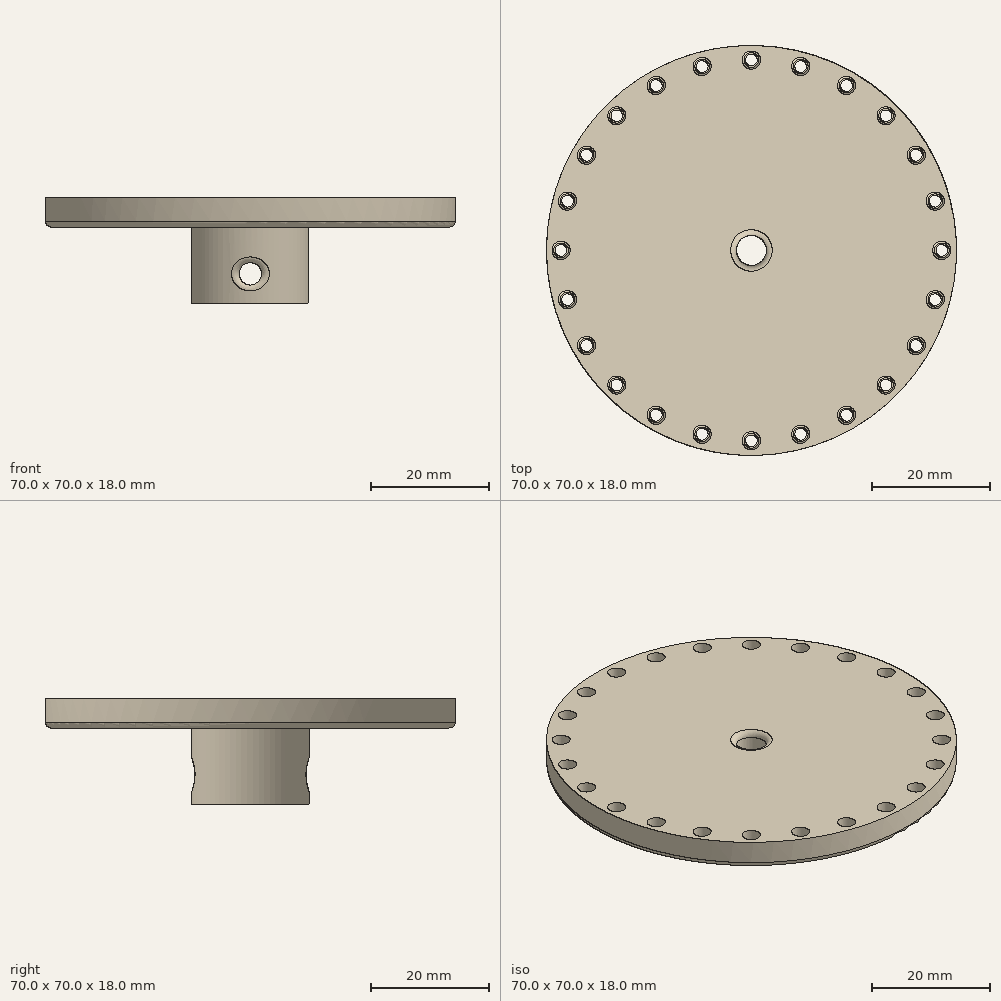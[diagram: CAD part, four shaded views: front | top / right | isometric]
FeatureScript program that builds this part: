
annotation { "Feature Type Name" : "Feature", "Feature Type Description" : "" }
export const myFeature = defineFeature(function(context is Context, id is Id, definition is map)
    precondition{}
    {
        {
            var Q0;
            Q0=qCreatedBy(makeId("Front.planeOp"),FACE);
            var sketch = newSketch(context, id + "F0", { "sketchPlane" : qUnion([Q0])});
            skLineSegment(sketch, "E0", {"start": v(0, 0) * mm, "end": v(0, 18) * mm, "construction": true});
            skLineSegment(sketch, "E1", {"start": v(0, 18) * mm, "end": v(35, 18) * mm});
            skLineSegment(sketch, "E2", {"start": v(35, 18) * mm, "end": v(35, 13) * mm});
            skLineSegment(sketch, "E3", {"start": v(35, 13) * mm, "end": v(10, 13) * mm});
            skLineSegment(sketch, "E4", {"start": v(10, 13) * mm, "end": v(10, 0) * mm});
            skLineSegment(sketch, "E5", {"start": v(10, 0) * mm, "end": v(0, 0) * mm});
            skLineSegment(sketch, "E6", {"start": v(0, 0) * mm, "end": v(0, 18) * mm});
            skSolve(sketch);
        }
        {
            var Q0;
            Q0=makeQuery(id+"F0.imprint","IMPRINT",FACE,{"disambiguationData":[TD([[makeQuery(id+"F0.imprint","IMPRINT",EDGE,{"derivedFrom":sQuery(id+"F0.wireOp",EDGE,"E1")}),-1.0]])]});
            var Q1;
            Q1=sQuery(id+"F0.wireOp",EDGE,"E6");
            revolve(context, id + "F1", {"entities" : qUnion([Q0]), "axis" : qUnion([Q1]), "revolveType" : RevolveType.FULL});
        }
        {
            var Q0;
            Q0=qCreatedBy(makeId("Front.planeOp"),FACE);
            var sketch = newSketch(context, id + "F2", { "sketchPlane" : qUnion([Q0])});
            skCircle(sketch, "E7", {"center": v(0, 5) * mm, "radius": 1.9 * mm});
            skSolve(sketch);
        }
        {
            var Q0;
            Q0 = qSketchRegion(id + "F2", true);
            extrude(context, id + "F3", {"entities" : qUnion([Q0]), "operationType" : NewBodyOperationType.REMOVE, "oppositeDirection" : true, "depth" : 25 * mm, "symmetric" : true});
        }
        {
            var Q0;
            Q0=makeQuery(id+"F1.opRevolve","SWEPT_FACE",FACE,{"disambiguationData":[OSD([sQuery(id+"F0.wireOp",EDGE,"E5")])]});
            var sketch = newSketch(context, id + "F4", { "sketchPlane" : qUnion([Q0])});
            skCircle(sketch, "E8", {"center": v(0, 0) * mm, "radius": 2.55 * mm});
            skSolve(sketch);
        }
        {
            var Q0;
            Q0 = qSketchRegion(id + "F4", true);
            extrude(context, id + "F5", {"entities" : qUnion([Q0]), "operationType" : NewBodyOperationType.REMOVE, "endBound" : BoundingType.THROUGH_ALL, "oppositeDirection" : true, "depth" : 25 * mm});
        }
        {
            var Q0;
            Q0=makeQuery(id+"F5.boolean.opBoolean","COPY",EDGE,{"derivedFrom":makeQuery(id+"F5.opExtrude","CAP_EDGE",EDGE,{"disambiguationData":[OSD([sQuery(id+"F4.wireOp",EDGE,"E8")])],"isStart":true})});
            var Q1;
            Q1=makeQuery(id+"F5.boolean.opBoolean","INTERSECT",EDGE,{"derivedFrom":[makeQuery(id+"F1.opRevolve","SWEPT_FACE",FACE,{"disambiguationData":[OSD([sQuery(id+"F0.wireOp",EDGE,"E1")])]}),makeQuery(id+"F5.opExtrude","SWEPT_FACE",FACE,{"disambiguationData":[OSD([sQuery(id+"F4.wireOp",EDGE,"E8")])]})]});
            var Q2;
            Q2=makeQuery(id+"F1.opRevolve","SWEPT_EDGE",EDGE,{"disambiguationData":[OSD([sQuery(id+"F0.wireOp",EDGE,"E2"),sQuery(id+"F0.wireOp",EDGE,"E3")])]});
            var Q3;
            Q3=makeQuery(id+"F3.boolean.opBoolean","INTERSECT",EDGE,{"disambiguationData":[OD(1.0)],"derivedFrom":[makeQuery(id+"F1.opRevolve","SWEPT_FACE",FACE,{"disambiguationData":[OSD([sQuery(id+"F0.wireOp",EDGE,"E4")])]}),makeQuery(id+"F3.opExtrude","SWEPT_FACE",FACE,{"disambiguationData":[OSD([sQuery(id+"F2.wireOp",EDGE,"E7")])]})]});
            var Q4;
            Q4=makeQuery(id+"F3.boolean.opBoolean","INTERSECT",EDGE,{"disambiguationData":[OD(0.0)],"derivedFrom":[makeQuery(id+"F1.opRevolve","SWEPT_FACE",FACE,{"disambiguationData":[OSD([sQuery(id+"F0.wireOp",EDGE,"E4")])]}),makeQuery(id+"F3.opExtrude","SWEPT_FACE",FACE,{"disambiguationData":[OSD([sQuery(id+"F2.wireOp",EDGE,"E7")])]})]});
            fillet(context, id + "F6", {"entities" : qUnion([Q0, Q1, Q2, Q3, Q4]), "radius" : 1 * mm, "tangentPropagation" : true, "allowEdgeOverflow" : false});
        }
        {
            var Q0;
            Q0=makeQuery(id+"F1.opRevolve","SWEPT_FACE",FACE,{"disambiguationData":[OSD([sQuery(id+"F0.wireOp",EDGE,"E1")])]});
            var sketch = newSketch(context, id + "F7", { "sketchPlane" : qUnion([Q0])});
            skCircle(sketch, "E9", {"center": v(-32.5, 0) * mm, "radius": 1.55 * mm});
            skCircle(sketch, "E10.1.0", {"center": v(-31.4, -8.41) * mm, "radius": 1.55 * mm});
            skCircle(sketch, "E10.2.0", {"center": v(-28.15, -16.25) * mm, "radius": 1.55 * mm});
            skCircle(sketch, "E10.3.0", {"center": v(-22.98, -22.98) * mm, "radius": 1.55 * mm});
            skCircle(sketch, "E10.4.0", {"center": v(-16.25, -28.15) * mm, "radius": 1.55 * mm});
            skCircle(sketch, "E10.5.0", {"center": v(-8.41, -31.4) * mm, "radius": 1.55 * mm});
            skCircle(sketch, "E10.6.0", {"center": v(0, -32.5) * mm, "radius": 1.55 * mm});
            skCircle(sketch, "E10.7.0", {"center": v(8.41, -31.4) * mm, "radius": 1.55 * mm});
            skCircle(sketch, "E10.8.0", {"center": v(16.25, -28.15) * mm, "radius": 1.55 * mm});
            skCircle(sketch, "E10.9.0", {"center": v(22.98, -22.98) * mm, "radius": 1.55 * mm});
            skCircle(sketch, "E10.10.0", {"center": v(28.15, -16.25) * mm, "radius": 1.55 * mm});
            skCircle(sketch, "E10.11.0", {"center": v(31.4, -8.41) * mm, "radius": 1.55 * mm});
            skCircle(sketch, "E10.12.0", {"center": v(32.5, 0) * mm, "radius": 1.55 * mm});
            skCircle(sketch, "E10.13.0", {"center": v(31.4, 8.41) * mm, "radius": 1.55 * mm});
            skCircle(sketch, "E10.14.0", {"center": v(28.15, 16.25) * mm, "radius": 1.55 * mm});
            skCircle(sketch, "E10.15.0", {"center": v(22.98, 22.98) * mm, "radius": 1.55 * mm});
            skCircle(sketch, "E10.16.0", {"center": v(16.25, 28.15) * mm, "radius": 1.55 * mm});
            skCircle(sketch, "E10.17.0", {"center": v(8.41, 31.4) * mm, "radius": 1.55 * mm});
            skCircle(sketch, "E10.18.0", {"center": v(0, 32.5) * mm, "radius": 1.55 * mm});
            skCircle(sketch, "E10.19.0", {"center": v(-8.41, 31.4) * mm, "radius": 1.55 * mm});
            skCircle(sketch, "E10.20.0", {"center": v(-16.25, 28.15) * mm, "radius": 1.55 * mm});
            skCircle(sketch, "E10.21.0", {"center": v(-22.98, 22.98) * mm, "radius": 1.55 * mm});
            skCircle(sketch, "E10.22.0", {"center": v(-28.15, 16.25) * mm, "radius": 1.55 * mm});
            skCircle(sketch, "E10.23.0", {"center": v(-31.4, 8.41) * mm, "radius": 1.55 * mm});
            skPoint(sketch, "E10.center", {"position": v(0, 0) * mm});
            skCircle(sketch, "E11", {"center": v(-32.5, 0) * mm, "radius": 1 * mm});
            skCircle(sketch, "E12.1.0", {"center": v(-31.4, -8.41) * mm, "radius": 1 * mm});
            skCircle(sketch, "E12.2.0", {"center": v(-28.15, -16.25) * mm, "radius": 1 * mm});
            skCircle(sketch, "E12.3.0", {"center": v(-22.98, -22.98) * mm, "radius": 1 * mm});
            skCircle(sketch, "E12.4.0", {"center": v(-16.25, -28.15) * mm, "radius": 1 * mm});
            skCircle(sketch, "E12.5.0", {"center": v(-8.41, -31.4) * mm, "radius": 1 * mm});
            skCircle(sketch, "E12.6.0", {"center": v(0, -32.5) * mm, "radius": 1 * mm});
            skCircle(sketch, "E12.7.0", {"center": v(8.41, -31.4) * mm, "radius": 1 * mm});
            skCircle(sketch, "E12.8.0", {"center": v(16.25, -28.15) * mm, "radius": 1 * mm});
            skCircle(sketch, "E12.9.0", {"center": v(22.98, -22.98) * mm, "radius": 1 * mm});
            skCircle(sketch, "E12.10.0", {"center": v(28.15, -16.25) * mm, "radius": 1 * mm});
            skCircle(sketch, "E12.11.0", {"center": v(31.4, -8.41) * mm, "radius": 1 * mm});
            skCircle(sketch, "E12.12.0", {"center": v(32.5, 0) * mm, "radius": 1 * mm});
            skCircle(sketch, "E12.13.0", {"center": v(31.4, 8.41) * mm, "radius": 1 * mm});
            skCircle(sketch, "E12.14.0", {"center": v(28.15, 16.25) * mm, "radius": 1 * mm});
            skCircle(sketch, "E12.15.0", {"center": v(22.98, 22.98) * mm, "radius": 1 * mm});
            skCircle(sketch, "E12.16.0", {"center": v(16.25, 28.15) * mm, "radius": 1 * mm});
            skCircle(sketch, "E12.17.0", {"center": v(8.41, 31.4) * mm, "radius": 1 * mm});
            skCircle(sketch, "E12.18.0", {"center": v(0, 32.5) * mm, "radius": 1 * mm});
            skCircle(sketch, "E12.19.0", {"center": v(-8.41, 31.4) * mm, "radius": 1 * mm});
            skCircle(sketch, "E12.20.0", {"center": v(-16.25, 28.15) * mm, "radius": 1 * mm});
            skCircle(sketch, "E12.21.0", {"center": v(-22.98, 22.98) * mm, "radius": 1 * mm});
            skCircle(sketch, "E12.22.0", {"center": v(-28.15, 16.25) * mm, "radius": 1 * mm});
            skCircle(sketch, "E12.23.0", {"center": v(-31.4, 8.41) * mm, "radius": 1 * mm});
            skSolve(sketch);
        }
        {
            var Q0;
            Q0=makeQuery(id+"F7.imprint","IMPRINT",FACE,{"disambiguationData":[TD([[makeQuery(id+"F7.imprint","IMPRINT",EDGE,{"derivedFrom":sQuery(id+"F7.wireOp",EDGE,"E10.20.0")}),1.0]])]});
            var Q1;
            Q1=makeQuery(id+"F7.imprint","IMPRINT",FACE,{"disambiguationData":[TD([[makeQuery(id+"F7.imprint","IMPRINT",EDGE,{"derivedFrom":sQuery(id+"F7.wireOp",EDGE,"E10.21.0")}),1.0]])]});
            var Q2;
            Q2=makeQuery(id+"F7.imprint","IMPRINT",FACE,{"disambiguationData":[TD([[makeQuery(id+"F7.imprint","IMPRINT",EDGE,{"derivedFrom":sQuery(id+"F7.wireOp",EDGE,"E10.22.0")}),1.0]])]});
            var Q3;
            Q3=makeQuery(id+"F7.imprint","IMPRINT",FACE,{"disambiguationData":[TD([[makeQuery(id+"F7.imprint","IMPRINT",EDGE,{"derivedFrom":sQuery(id+"F7.wireOp",EDGE,"E10.23.0")}),1.0]])]});
            var Q4;
            Q4=makeQuery(id+"F7.imprint","IMPRINT",FACE,{"disambiguationData":[TD([[makeQuery(id+"F7.imprint","IMPRINT",EDGE,{"derivedFrom":sQuery(id+"F7.wireOp",EDGE,"E10.19.0")}),1.0]])]});
            var Q5;
            Q5=makeQuery(id+"F7.imprint","IMPRINT",FACE,{"disambiguationData":[TD([[makeQuery(id+"F7.imprint","IMPRINT",EDGE,{"derivedFrom":sQuery(id+"F7.wireOp",EDGE,"E10.18.0")}),1.0]])]});
            var Q6;
            Q6=makeQuery(id+"F7.imprint","IMPRINT",FACE,{"disambiguationData":[TD([[makeQuery(id+"F7.imprint","IMPRINT",EDGE,{"derivedFrom":sQuery(id+"F7.wireOp",EDGE,"E10.17.0")}),1.0]])]});
            var Q7;
            Q7=makeQuery(id+"F7.imprint","IMPRINT",FACE,{"disambiguationData":[TD([[makeQuery(id+"F7.imprint","IMPRINT",EDGE,{"derivedFrom":sQuery(id+"F7.wireOp",EDGE,"E10.16.0")}),1.0]])]});
            var Q8;
            Q8=makeQuery(id+"F7.imprint","IMPRINT",FACE,{"disambiguationData":[TD([[makeQuery(id+"F7.imprint","IMPRINT",EDGE,{"derivedFrom":sQuery(id+"F7.wireOp",EDGE,"E10.15.0")}),1.0]])]});
            var Q9;
            Q9=makeQuery(id+"F7.imprint","IMPRINT",FACE,{"disambiguationData":[TD([[makeQuery(id+"F7.imprint","IMPRINT",EDGE,{"derivedFrom":sQuery(id+"F7.wireOp",EDGE,"E10.1.0")}),1.0]])]});
            var Q10;
            Q10=makeQuery(id+"F7.imprint","IMPRINT",FACE,{"disambiguationData":[TD([[makeQuery(id+"F7.imprint","IMPRINT",EDGE,{"derivedFrom":sQuery(id+"F7.wireOp",EDGE,"E10.2.0")}),1.0]])]});
            var Q11;
            Q11=makeQuery(id+"F7.imprint","IMPRINT",FACE,{"disambiguationData":[TD([[makeQuery(id+"F7.imprint","IMPRINT",EDGE,{"derivedFrom":sQuery(id+"F7.wireOp",EDGE,"E10.3.0")}),1.0]])]});
            var Q12;
            Q12=makeQuery(id+"F7.imprint","IMPRINT",FACE,{"disambiguationData":[TD([[makeQuery(id+"F7.imprint","IMPRINT",EDGE,{"derivedFrom":sQuery(id+"F7.wireOp",EDGE,"E10.4.0")}),1.0]])]});
            var Q13;
            Q13=makeQuery(id+"F7.imprint","IMPRINT",FACE,{"disambiguationData":[TD([[makeQuery(id+"F7.imprint","IMPRINT",EDGE,{"derivedFrom":sQuery(id+"F7.wireOp",EDGE,"E10.5.0")}),1.0]])]});
            var Q14;
            Q14=makeQuery(id+"F7.imprint","IMPRINT",FACE,{"disambiguationData":[TD([[makeQuery(id+"F7.imprint","IMPRINT",EDGE,{"derivedFrom":sQuery(id+"F7.wireOp",EDGE,"E10.6.0")}),1.0]])]});
            var Q15;
            Q15=makeQuery(id+"F7.imprint","IMPRINT",FACE,{"disambiguationData":[TD([[makeQuery(id+"F7.imprint","IMPRINT",EDGE,{"derivedFrom":sQuery(id+"F7.wireOp",EDGE,"E10.7.0")}),1.0]])]});
            var Q16;
            Q16=makeQuery(id+"F7.imprint","IMPRINT",FACE,{"disambiguationData":[TD([[makeQuery(id+"F7.imprint","IMPRINT",EDGE,{"derivedFrom":sQuery(id+"F7.wireOp",EDGE,"E10.8.0")}),1.0]])]});
            var Q17;
            Q17=makeQuery(id+"F7.imprint","IMPRINT",FACE,{"disambiguationData":[TD([[makeQuery(id+"F7.imprint","IMPRINT",EDGE,{"derivedFrom":sQuery(id+"F7.wireOp",EDGE,"E10.9.0")}),1.0]])]});
            var Q18;
            Q18=makeQuery(id+"F7.imprint","IMPRINT",FACE,{"disambiguationData":[TD([[makeQuery(id+"F7.imprint","IMPRINT",EDGE,{"derivedFrom":sQuery(id+"F7.wireOp",EDGE,"E10.10.0")}),1.0]])]});
            var Q19;
            Q19=makeQuery(id+"F7.imprint","IMPRINT",FACE,{"disambiguationData":[TD([[makeQuery(id+"F7.imprint","IMPRINT",EDGE,{"derivedFrom":sQuery(id+"F7.wireOp",EDGE,"E10.11.0")}),1.0]])]});
            var Q20;
            Q20=makeQuery(id+"F7.imprint","IMPRINT",FACE,{"disambiguationData":[TD([[makeQuery(id+"F7.imprint","IMPRINT",EDGE,{"derivedFrom":sQuery(id+"F7.wireOp",EDGE,"E10.12.0")}),1.0]])]});
            var Q21;
            Q21=makeQuery(id+"F7.imprint","IMPRINT",FACE,{"disambiguationData":[TD([[makeQuery(id+"F7.imprint","IMPRINT",EDGE,{"derivedFrom":sQuery(id+"F7.wireOp",EDGE,"E10.13.0")}),1.0]])]});
            var Q22;
            Q22=makeQuery(id+"F7.imprint","IMPRINT",FACE,{"disambiguationData":[TD([[makeQuery(id+"F7.imprint","IMPRINT",EDGE,{"derivedFrom":sQuery(id+"F7.wireOp",EDGE,"E10.14.0")}),1.0]])]});
            var Q23;
            Q23=makeQuery(id+"F7.imprint","IMPRINT",FACE,{"disambiguationData":[TD([[makeQuery(id+"F7.imprint","IMPRINT",EDGE,{"derivedFrom":sQuery(id+"F7.wireOp",EDGE,"E9")}),1.0]])]});
            extrude(context, id + "F8", {"entities" : qUnion([Q0, Q1, Q2, Q3, Q4, Q5, Q6, Q7, Q8, Q9, Q10, Q11, Q12, Q13, Q14, Q15, Q16, Q17, Q18, Q19, Q20, Q21, Q22, Q23]), "operationType" : NewBodyOperationType.REMOVE, "oppositeDirection" : true, "depth" : 4.5 * mm});
        }
        {
            var Q0;
            Q0=makeQuery(id+"F8.boolean.opBoolean","SPLIT",FACE,{"disambiguationData":[TD([makeQuery(id+"F8.opExtrude","SWEPT_FACE",FACE,{"disambiguationData":[OSD([sQuery(id+"F7.wireOp",EDGE,"E12.23.0")])]})])],"derivedFrom":makeQuery(id+"F1.opRevolve","SWEPT_FACE",FACE,{"disambiguationData":[OSD([sQuery(id+"F0.wireOp",EDGE,"E1")])]})});
            var Q1;
            Q1=makeQuery(id+"F8.boolean.opBoolean","SPLIT",FACE,{"disambiguationData":[TD([makeQuery(id+"F8.opExtrude","SWEPT_FACE",FACE,{"disambiguationData":[OSD([sQuery(id+"F7.wireOp",EDGE,"E12.22.0")])]})])],"derivedFrom":makeQuery(id+"F1.opRevolve","SWEPT_FACE",FACE,{"disambiguationData":[OSD([sQuery(id+"F0.wireOp",EDGE,"E1")])]})});
            var Q2;
            Q2=makeQuery(id+"F8.boolean.opBoolean","SPLIT",FACE,{"disambiguationData":[TD([makeQuery(id+"F8.opExtrude","SWEPT_FACE",FACE,{"disambiguationData":[OSD([sQuery(id+"F7.wireOp",EDGE,"E12.21.0")])]})])],"derivedFrom":makeQuery(id+"F1.opRevolve","SWEPT_FACE",FACE,{"disambiguationData":[OSD([sQuery(id+"F0.wireOp",EDGE,"E1")])]})});
            var Q3;
            Q3=makeQuery(id+"F8.boolean.opBoolean","SPLIT",FACE,{"disambiguationData":[TD([makeQuery(id+"F8.opExtrude","SWEPT_FACE",FACE,{"disambiguationData":[OSD([sQuery(id+"F7.wireOp",EDGE,"E12.20.0")])]})])],"derivedFrom":makeQuery(id+"F1.opRevolve","SWEPT_FACE",FACE,{"disambiguationData":[OSD([sQuery(id+"F0.wireOp",EDGE,"E1")])]})});
            var Q4;
            Q4=makeQuery(id+"F8.boolean.opBoolean","SPLIT",FACE,{"disambiguationData":[TD([makeQuery(id+"F8.opExtrude","SWEPT_FACE",FACE,{"disambiguationData":[OSD([sQuery(id+"F7.wireOp",EDGE,"E12.19.0")])]})])],"derivedFrom":makeQuery(id+"F1.opRevolve","SWEPT_FACE",FACE,{"disambiguationData":[OSD([sQuery(id+"F0.wireOp",EDGE,"E1")])]})});
            var Q5;
            Q5=makeQuery(id+"F8.boolean.opBoolean","SPLIT",FACE,{"disambiguationData":[TD([makeQuery(id+"F8.opExtrude","SWEPT_FACE",FACE,{"disambiguationData":[OSD([sQuery(id+"F7.wireOp",EDGE,"E12.18.0")])]})])],"derivedFrom":makeQuery(id+"F1.opRevolve","SWEPT_FACE",FACE,{"disambiguationData":[OSD([sQuery(id+"F0.wireOp",EDGE,"E1")])]})});
            var Q6;
            Q6=makeQuery(id+"F8.boolean.opBoolean","SPLIT",FACE,{"disambiguationData":[TD([makeQuery(id+"F8.opExtrude","SWEPT_FACE",FACE,{"disambiguationData":[OSD([sQuery(id+"F7.wireOp",EDGE,"E12.17.0")])]})])],"derivedFrom":makeQuery(id+"F1.opRevolve","SWEPT_FACE",FACE,{"disambiguationData":[OSD([sQuery(id+"F0.wireOp",EDGE,"E1")])]})});
            var Q7;
            Q7=makeQuery(id+"F8.boolean.opBoolean","SPLIT",FACE,{"disambiguationData":[TD([makeQuery(id+"F8.opExtrude","SWEPT_FACE",FACE,{"disambiguationData":[OSD([sQuery(id+"F7.wireOp",EDGE,"E12.16.0")])]})])],"derivedFrom":makeQuery(id+"F1.opRevolve","SWEPT_FACE",FACE,{"disambiguationData":[OSD([sQuery(id+"F0.wireOp",EDGE,"E1")])]})});
            var Q8;
            Q8=makeQuery(id+"F8.boolean.opBoolean","SPLIT",FACE,{"disambiguationData":[TD([makeQuery(id+"F8.opExtrude","SWEPT_FACE",FACE,{"disambiguationData":[OSD([sQuery(id+"F7.wireOp",EDGE,"E11")])]})])],"derivedFrom":makeQuery(id+"F1.opRevolve","SWEPT_FACE",FACE,{"disambiguationData":[OSD([sQuery(id+"F0.wireOp",EDGE,"E1")])]})});
            var Q9;
            Q9=makeQuery(id+"F8.boolean.opBoolean","SPLIT",FACE,{"disambiguationData":[TD([makeQuery(id+"F8.opExtrude","SWEPT_FACE",FACE,{"disambiguationData":[OSD([sQuery(id+"F7.wireOp",EDGE,"E12.1.0")])]})])],"derivedFrom":makeQuery(id+"F1.opRevolve","SWEPT_FACE",FACE,{"disambiguationData":[OSD([sQuery(id+"F0.wireOp",EDGE,"E1")])]})});
            var Q10;
            Q10=makeQuery(id+"F8.boolean.opBoolean","SPLIT",FACE,{"disambiguationData":[TD([makeQuery(id+"F8.opExtrude","SWEPT_FACE",FACE,{"disambiguationData":[OSD([sQuery(id+"F7.wireOp",EDGE,"E12.2.0")])]})])],"derivedFrom":makeQuery(id+"F1.opRevolve","SWEPT_FACE",FACE,{"disambiguationData":[OSD([sQuery(id+"F0.wireOp",EDGE,"E1")])]})});
            var Q11;
            Q11=makeQuery(id+"F8.boolean.opBoolean","SPLIT",FACE,{"disambiguationData":[TD([makeQuery(id+"F8.opExtrude","SWEPT_FACE",FACE,{"disambiguationData":[OSD([sQuery(id+"F7.wireOp",EDGE,"E12.3.0")])]})])],"derivedFrom":makeQuery(id+"F1.opRevolve","SWEPT_FACE",FACE,{"disambiguationData":[OSD([sQuery(id+"F0.wireOp",EDGE,"E1")])]})});
            var Q12;
            Q12=makeQuery(id+"F8.boolean.opBoolean","SPLIT",FACE,{"disambiguationData":[TD([makeQuery(id+"F8.opExtrude","SWEPT_FACE",FACE,{"disambiguationData":[OSD([sQuery(id+"F7.wireOp",EDGE,"E12.4.0")])]})])],"derivedFrom":makeQuery(id+"F1.opRevolve","SWEPT_FACE",FACE,{"disambiguationData":[OSD([sQuery(id+"F0.wireOp",EDGE,"E1")])]})});
            var Q13;
            Q13=makeQuery(id+"F8.boolean.opBoolean","SPLIT",FACE,{"disambiguationData":[TD([makeQuery(id+"F8.opExtrude","SWEPT_FACE",FACE,{"disambiguationData":[OSD([sQuery(id+"F7.wireOp",EDGE,"E12.5.0")])]})])],"derivedFrom":makeQuery(id+"F1.opRevolve","SWEPT_FACE",FACE,{"disambiguationData":[OSD([sQuery(id+"F0.wireOp",EDGE,"E1")])]})});
            var Q14;
            Q14=makeQuery(id+"F8.boolean.opBoolean","SPLIT",FACE,{"disambiguationData":[TD([makeQuery(id+"F8.opExtrude","SWEPT_FACE",FACE,{"disambiguationData":[OSD([sQuery(id+"F7.wireOp",EDGE,"E12.6.0")])]})])],"derivedFrom":makeQuery(id+"F1.opRevolve","SWEPT_FACE",FACE,{"disambiguationData":[OSD([sQuery(id+"F0.wireOp",EDGE,"E1")])]})});
            var Q15;
            Q15=makeQuery(id+"F8.boolean.opBoolean","SPLIT",FACE,{"disambiguationData":[TD([makeQuery(id+"F8.opExtrude","SWEPT_FACE",FACE,{"disambiguationData":[OSD([sQuery(id+"F7.wireOp",EDGE,"E12.7.0")])]})])],"derivedFrom":makeQuery(id+"F1.opRevolve","SWEPT_FACE",FACE,{"disambiguationData":[OSD([sQuery(id+"F0.wireOp",EDGE,"E1")])]})});
            var Q16;
            Q16=makeQuery(id+"F8.boolean.opBoolean","SPLIT",FACE,{"disambiguationData":[TD([makeQuery(id+"F8.opExtrude","SWEPT_FACE",FACE,{"disambiguationData":[OSD([sQuery(id+"F7.wireOp",EDGE,"E12.8.0")])]})])],"derivedFrom":makeQuery(id+"F1.opRevolve","SWEPT_FACE",FACE,{"disambiguationData":[OSD([sQuery(id+"F0.wireOp",EDGE,"E1")])]})});
            var Q17;
            Q17=makeQuery(id+"F8.boolean.opBoolean","SPLIT",FACE,{"disambiguationData":[TD([makeQuery(id+"F8.opExtrude","SWEPT_FACE",FACE,{"disambiguationData":[OSD([sQuery(id+"F7.wireOp",EDGE,"E12.9.0")])]})])],"derivedFrom":makeQuery(id+"F1.opRevolve","SWEPT_FACE",FACE,{"disambiguationData":[OSD([sQuery(id+"F0.wireOp",EDGE,"E1")])]})});
            var Q18;
            Q18=makeQuery(id+"F8.boolean.opBoolean","SPLIT",FACE,{"disambiguationData":[TD([makeQuery(id+"F8.opExtrude","SWEPT_FACE",FACE,{"disambiguationData":[OSD([sQuery(id+"F7.wireOp",EDGE,"E12.10.0")])]})])],"derivedFrom":makeQuery(id+"F1.opRevolve","SWEPT_FACE",FACE,{"disambiguationData":[OSD([sQuery(id+"F0.wireOp",EDGE,"E1")])]})});
            var Q19;
            Q19=makeQuery(id+"F8.boolean.opBoolean","SPLIT",FACE,{"disambiguationData":[TD([makeQuery(id+"F8.opExtrude","SWEPT_FACE",FACE,{"disambiguationData":[OSD([sQuery(id+"F7.wireOp",EDGE,"E12.11.0")])]})])],"derivedFrom":makeQuery(id+"F1.opRevolve","SWEPT_FACE",FACE,{"disambiguationData":[OSD([sQuery(id+"F0.wireOp",EDGE,"E1")])]})});
            var Q20;
            Q20=makeQuery(id+"F8.boolean.opBoolean","SPLIT",FACE,{"disambiguationData":[TD([makeQuery(id+"F8.opExtrude","SWEPT_FACE",FACE,{"disambiguationData":[OSD([sQuery(id+"F7.wireOp",EDGE,"E12.12.0")])]})])],"derivedFrom":makeQuery(id+"F1.opRevolve","SWEPT_FACE",FACE,{"disambiguationData":[OSD([sQuery(id+"F0.wireOp",EDGE,"E1")])]})});
            var Q21;
            Q21=makeQuery(id+"F8.boolean.opBoolean","SPLIT",FACE,{"disambiguationData":[TD([makeQuery(id+"F8.opExtrude","SWEPT_FACE",FACE,{"disambiguationData":[OSD([sQuery(id+"F7.wireOp",EDGE,"E12.13.0")])]})])],"derivedFrom":makeQuery(id+"F1.opRevolve","SWEPT_FACE",FACE,{"disambiguationData":[OSD([sQuery(id+"F0.wireOp",EDGE,"E1")])]})});
            var Q22;
            Q22=makeQuery(id+"F8.boolean.opBoolean","SPLIT",FACE,{"disambiguationData":[TD([makeQuery(id+"F8.opExtrude","SWEPT_FACE",FACE,{"disambiguationData":[OSD([sQuery(id+"F7.wireOp",EDGE,"E12.14.0")])]})])],"derivedFrom":makeQuery(id+"F1.opRevolve","SWEPT_FACE",FACE,{"disambiguationData":[OSD([sQuery(id+"F0.wireOp",EDGE,"E1")])]})});
            var Q23;
            Q23=makeQuery(id+"F8.boolean.opBoolean","SPLIT",FACE,{"disambiguationData":[TD([makeQuery(id+"F8.opExtrude","SWEPT_FACE",FACE,{"disambiguationData":[OSD([sQuery(id+"F7.wireOp",EDGE,"E12.15.0")])]})])],"derivedFrom":makeQuery(id+"F1.opRevolve","SWEPT_FACE",FACE,{"disambiguationData":[OSD([sQuery(id+"F0.wireOp",EDGE,"E1")])]})});
            extrude(context, id + "F9", {"entities" : qUnion([Q0, Q1, Q2, Q3, Q4, Q5, Q6, Q7, Q8, Q9, Q10, Q11, Q12, Q13, Q14, Q15, Q16, Q17, Q18, Q19, Q20, Q21, Q22, Q23]), "operationType" : NewBodyOperationType.REMOVE, "oppositeDirection" : true, "depth" : 25 * mm});
        }
        {
            var Q0;
            Q0=makeQuery(id+"F8.boolean.opBoolean","COPY",EDGE,{"derivedFrom":makeQuery(id+"F8.opExtrude","CAP_EDGE",EDGE,{"disambiguationData":[OSD([sQuery(id+"F7.wireOp",EDGE,"E10.11.0")])],"isStart":false})});
            var Q1;
            Q1=makeQuery(id+"F8.boolean.opBoolean","COPY",EDGE,{"derivedFrom":makeQuery(id+"F8.opExtrude","CAP_EDGE",EDGE,{"disambiguationData":[OSD([sQuery(id+"F7.wireOp",EDGE,"E10.12.0")])],"isStart":false})});
            var Q2;
            Q2=makeQuery(id+"F8.boolean.opBoolean","COPY",EDGE,{"derivedFrom":makeQuery(id+"F8.opExtrude","CAP_EDGE",EDGE,{"disambiguationData":[OSD([sQuery(id+"F7.wireOp",EDGE,"E10.13.0")])],"isStart":false})});
            var Q3;
            Q3=makeQuery(id+"F8.boolean.opBoolean","COPY",EDGE,{"derivedFrom":makeQuery(id+"F8.opExtrude","CAP_EDGE",EDGE,{"disambiguationData":[OSD([sQuery(id+"F7.wireOp",EDGE,"E10.14.0")])],"isStart":false})});
            var Q4;
            Q4=makeQuery(id+"F8.boolean.opBoolean","COPY",EDGE,{"derivedFrom":makeQuery(id+"F8.opExtrude","CAP_EDGE",EDGE,{"disambiguationData":[OSD([sQuery(id+"F7.wireOp",EDGE,"E10.15.0")])],"isStart":false})});
            var Q5;
            Q5=makeQuery(id+"F8.boolean.opBoolean","COPY",EDGE,{"derivedFrom":makeQuery(id+"F8.opExtrude","CAP_EDGE",EDGE,{"disambiguationData":[OSD([sQuery(id+"F7.wireOp",EDGE,"E10.16.0")])],"isStart":false})});
            var Q6;
            Q6=makeQuery(id+"F8.boolean.opBoolean","COPY",EDGE,{"derivedFrom":makeQuery(id+"F8.opExtrude","CAP_EDGE",EDGE,{"disambiguationData":[OSD([sQuery(id+"F7.wireOp",EDGE,"E10.17.0")])],"isStart":false})});
            var Q7;
            Q7=makeQuery(id+"F8.boolean.opBoolean","COPY",EDGE,{"derivedFrom":makeQuery(id+"F8.opExtrude","CAP_EDGE",EDGE,{"disambiguationData":[OSD([sQuery(id+"F7.wireOp",EDGE,"E10.18.0")])],"isStart":false})});
            var Q8;
            Q8=makeQuery(id+"F8.boolean.opBoolean","COPY",EDGE,{"derivedFrom":makeQuery(id+"F8.opExtrude","CAP_EDGE",EDGE,{"disambiguationData":[OSD([sQuery(id+"F7.wireOp",EDGE,"E10.19.0")])],"isStart":false})});
            var Q9;
            Q9=makeQuery(id+"F8.boolean.opBoolean","COPY",EDGE,{"derivedFrom":makeQuery(id+"F8.opExtrude","CAP_EDGE",EDGE,{"disambiguationData":[OSD([sQuery(id+"F7.wireOp",EDGE,"E10.20.0")])],"isStart":false})});
            var Q10;
            Q10=makeQuery(id+"F8.boolean.opBoolean","COPY",EDGE,{"derivedFrom":makeQuery(id+"F8.opExtrude","CAP_EDGE",EDGE,{"disambiguationData":[OSD([sQuery(id+"F7.wireOp",EDGE,"E10.21.0")])],"isStart":false})});
            var Q11;
            Q11=makeQuery(id+"F8.boolean.opBoolean","COPY",EDGE,{"derivedFrom":makeQuery(id+"F8.opExtrude","CAP_EDGE",EDGE,{"disambiguationData":[OSD([sQuery(id+"F7.wireOp",EDGE,"E10.22.0")])],"isStart":false})});
            var Q12;
            Q12=makeQuery(id+"F8.boolean.opBoolean","COPY",EDGE,{"derivedFrom":makeQuery(id+"F8.opExtrude","CAP_EDGE",EDGE,{"disambiguationData":[OSD([sQuery(id+"F7.wireOp",EDGE,"E10.23.0")])],"isStart":false})});
            var Q13;
            Q13=makeQuery(id+"F8.boolean.opBoolean","COPY",EDGE,{"derivedFrom":makeQuery(id+"F8.opExtrude","CAP_EDGE",EDGE,{"disambiguationData":[OSD([sQuery(id+"F7.wireOp",EDGE,"E9")])],"isStart":false})});
            var Q14;
            Q14=makeQuery(id+"F8.boolean.opBoolean","COPY",EDGE,{"derivedFrom":makeQuery(id+"F8.opExtrude","CAP_EDGE",EDGE,{"disambiguationData":[OSD([sQuery(id+"F7.wireOp",EDGE,"E10.1.0")])],"isStart":false})});
            var Q15;
            Q15=makeQuery(id+"F8.boolean.opBoolean","COPY",EDGE,{"derivedFrom":makeQuery(id+"F8.opExtrude","CAP_EDGE",EDGE,{"disambiguationData":[OSD([sQuery(id+"F7.wireOp",EDGE,"E10.2.0")])],"isStart":false})});
            var Q16;
            Q16=makeQuery(id+"F8.boolean.opBoolean","COPY",EDGE,{"derivedFrom":makeQuery(id+"F8.opExtrude","CAP_EDGE",EDGE,{"disambiguationData":[OSD([sQuery(id+"F7.wireOp",EDGE,"E10.3.0")])],"isStart":false})});
            var Q17;
            Q17=makeQuery(id+"F8.boolean.opBoolean","COPY",EDGE,{"derivedFrom":makeQuery(id+"F8.opExtrude","CAP_EDGE",EDGE,{"disambiguationData":[OSD([sQuery(id+"F7.wireOp",EDGE,"E10.4.0")])],"isStart":false})});
            var Q18;
            Q18=makeQuery(id+"F8.boolean.opBoolean","COPY",EDGE,{"derivedFrom":makeQuery(id+"F8.opExtrude","CAP_EDGE",EDGE,{"disambiguationData":[OSD([sQuery(id+"F7.wireOp",EDGE,"E10.5.0")])],"isStart":false})});
            var Q19;
            Q19=makeQuery(id+"F8.boolean.opBoolean","COPY",EDGE,{"derivedFrom":makeQuery(id+"F8.opExtrude","CAP_EDGE",EDGE,{"disambiguationData":[OSD([sQuery(id+"F7.wireOp",EDGE,"E10.6.0")])],"isStart":false})});
            var Q20;
            Q20=makeQuery(id+"F8.boolean.opBoolean","COPY",EDGE,{"derivedFrom":makeQuery(id+"F8.opExtrude","CAP_EDGE",EDGE,{"disambiguationData":[OSD([sQuery(id+"F7.wireOp",EDGE,"E10.7.0")])],"isStart":false})});
            var Q21;
            Q21=makeQuery(id+"F8.boolean.opBoolean","COPY",EDGE,{"derivedFrom":makeQuery(id+"F8.opExtrude","CAP_EDGE",EDGE,{"disambiguationData":[OSD([sQuery(id+"F7.wireOp",EDGE,"E10.8.0")])],"isStart":false})});
            var Q22;
            Q22=makeQuery(id+"F8.boolean.opBoolean","COPY",EDGE,{"derivedFrom":makeQuery(id+"F8.opExtrude","CAP_EDGE",EDGE,{"disambiguationData":[OSD([sQuery(id+"F7.wireOp",EDGE,"E10.9.0")])],"isStart":false})});
            var Q23;
            Q23=makeQuery(id+"F8.boolean.opBoolean","COPY",EDGE,{"derivedFrom":makeQuery(id+"F8.opExtrude","CAP_EDGE",EDGE,{"disambiguationData":[OSD([sQuery(id+"F7.wireOp",EDGE,"E10.10.0")])],"isStart":false})});
            chamfer(context, id + "F10", {"entities" : qUnion([Q0, Q1, Q2, Q3, Q4, Q5, Q6, Q7, Q8, Q9, Q10, Q11, Q12, Q13, Q14, Q15, Q16, Q17, Q18, Q19, Q20, Q21, Q22, Q23]), "width" : 0.3 * mm, "tangentPropagation" : true});
        }
    });
